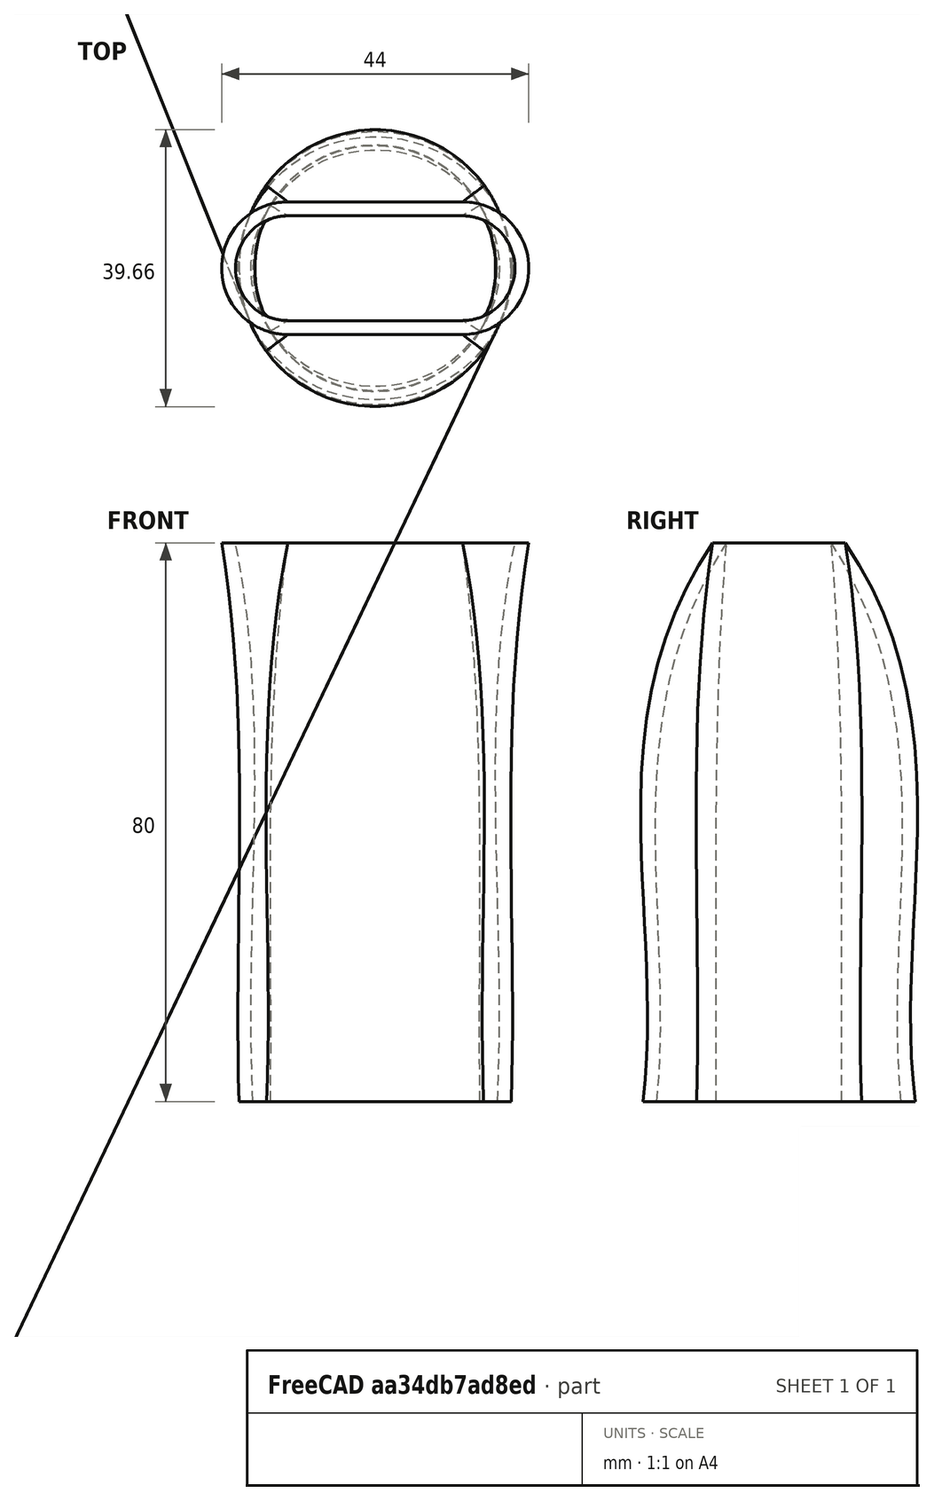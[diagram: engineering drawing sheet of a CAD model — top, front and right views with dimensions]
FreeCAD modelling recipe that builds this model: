
FCSTD DOCUMENT  (FreeCAD 2021.911R24301 +3846 (Git))
Label: nozzle
License: All rights reserved
LicenseURL: http://en.wikipedia.org/wiki/All_rights_reserved
objects: Sketcher::SketchObject×4, PartDesign::AdditiveLoft×1, PartDesign::Body×1
note: 8 computed .brp shape members not serialized (recipe doc carries the construction recipe); baked Part::Feature solids carry a one-line shape summary decoded from their .brp

FEATURE [Sketcher::SketchObject] Sketch
  FullyConstrained = true
  MapMode = 5
  Support = -> [XY_Plane]
  sketch-geometry (2):
    g0: Circle CenterX=0 CenterY=0 CenterZ=0 NormalX=0 NormalY=0 NormalZ=1 AngleXU=0 Radius=17.5
    g1: Circle CenterX=0 CenterY=0 CenterZ=0 NormalX=0 NormalY=0 NormalZ=1 AngleXU=0 Radius=19.5
  constraints (4):
    c: Coincident(g0,g-1)
    c: Diameter(g0) = 35
    c: Coincident(g1,g0)
    c: Diameter(g1) = 39
FEATURE [Sketcher::SketchObject] Sketch001
  AttachmentOffset = pos=(0,0,30) rot=(0,0,1;0rad)
  FullyConstrained = true
  MapMode = 5
  Placement = pos=(0,0,30) rot=(0,0,1;0rad)
  Support = -> [XY_Plane]
  sketch-geometry (2):
    g0: Circle CenterX=0 CenterY=0 CenterZ=0 NormalX=0 NormalY=0 NormalZ=1 AngleXU=0 Radius=17.5
    g1: Circle CenterX=0 CenterY=0 CenterZ=0 NormalX=0 NormalY=0 NormalZ=1 AngleXU=0 Radius=19.5
  constraints (4):
    c: Coincident(g0,g-1)
    c: Diameter(g0) = 35
    c: Coincident(g1,g0)
    c: Diameter(g1) = 39
FEATURE [Sketcher::SketchObject] Sketch002
  AttachmentOffset = pos=(0,0,50) rot=(0,0,1;0rad)
  FullyConstrained = true
  MapMode = 5
  Placement = pos=(0,0,50) rot=(0,0,1;0rad)
  Support = -> [XY_Plane]
  sketch-geometry (2):
    g0: Circle CenterX=0 CenterY=0 CenterZ=0 NormalX=0 NormalY=0 NormalZ=1 AngleXU=0 Radius=17.25
    g1: Circle CenterX=0 CenterY=0 CenterZ=0 NormalX=0 NormalY=0 NormalZ=1 AngleXU=0 Radius=19.5
  constraints (4):
    c: Coincident(g0,g-1)
    c: Diameter(g0) = 34.5
    c: Coincident(g1,g0)
    c: Diameter(g1) = 39
FEATURE [Sketcher::SketchObject] Sketch003
  AttachmentOffset = pos=(0,0,80) rot=(0,0,1;0rad)
  FullyConstrained = true
  MapMode = 5
  Placement = pos=(0,0,80) rot=(0,0,1;0rad)
  Support = -> [XY_Plane]
  sketch-geometry (9):
    g0: ArcOfCircle CenterX=-12.5 CenterY=0 CenterZ=0 NormalX=0 NormalY=0 NormalZ=1 AngleXU=0 Radius=7.5 StartAngle=1.5708 EndAngle=4.71239
    g1: ArcOfCircle CenterX=12.5 CenterY=0 CenterZ=0 NormalX=0 NormalY=0 NormalZ=1 AngleXU=0 Radius=7.5 StartAngle=4.71239 EndAngle=7.85398
    g2: LineSegment StartX=-12.5 StartY=-7.5 StartZ=0 EndX=12.5 EndY=-7.5 EndZ=0
    g3: LineSegment StartX=-12.5 StartY=7.5 StartZ=0 EndX=12.5 EndY=7.5 EndZ=0
    g4: LineSegment [constr] StartX=20 StartY=0 StartZ=0 EndX=-20 EndY=0 EndZ=0
    g5: ArcOfCircle CenterX=-12.5 CenterY=0 CenterZ=0 NormalX=0 NormalY=0 NormalZ=1 AngleXU=0 Radius=9.5 StartAngle=1.5708 EndAngle=4.71239
    g6: ArcOfCircle CenterX=12.5 CenterY=0 CenterZ=0 NormalX=0 NormalY=0 NormalZ=1 AngleXU=0 Radius=9.5 StartAngle=4.71239 EndAngle=7.85398
    g7: LineSegment StartX=-12.5 StartY=-9.5 StartZ=0 EndX=12.5 EndY=-9.5 EndZ=0
    g8: LineSegment StartX=-12.5 StartY=9.5 StartZ=0 EndX=12.5 EndY=9.5 EndZ=0
  constraints (21):
    c: Tangent(g0,g3) = 1.5708
    c: Tangent(g0,g2) = -1.5708
    c: Tangent(g2,g1) = -1.5708
    c: Tangent(g3,g1) = 1.5708
    c: Horizontal(g2)
    c: PointOnObject(g0,g-1)
    c: Symmetric(g1,g0,g-2)
    c: DistanceY(g1,g1) = 15
    c: PointOnObject(g4,g1)
    c: PointOnObject(g4,g0)
    c: Horizontal(g4)
    c: PointOnObject(g4,g-1)
    c: DistanceX(g4,g4) = 40
    c: Tangent(g5,g8) = 1.5708
    c: Tangent(g5,g7) = -1.5708
    c: Tangent(g7,g6) = -1.5708
    c: Tangent(g8,g6) = 1.5708
    c: Horizontal(g7)
    c: Coincident(g5,g0)
    c: Coincident(g6,g1)
    c: Diameter(g6) = 19
FEATURE [PartDesign::AdditiveLoft] AdditiveLoft
  ClaimChildren = false
  Closed = false
  Fit = 0
  FitJoin = 0
  InnerFit = 0
  InnerFitJoin = 0
  NewSolid = false
  Profile = -> Sketch
  Refine = true
  Ruled = false
  Sections = -> [Sketch001,Sketch002,Sketch003]
  Suppress = false
  _ProfileBasedVersion = 1
FEATURE [PartDesign::Body] Body
  AutoGroupSolids = false
  ExportMode = 0
  Group = -> [Sketch,Sketch001,Sketch002,Sketch003,AdditiveLoft]
  Origin = -> Origin
  Tip = -> AdditiveLoft
  _ExportChildren = -> [AdditiveLoft]
  _GroupVersion = 1
